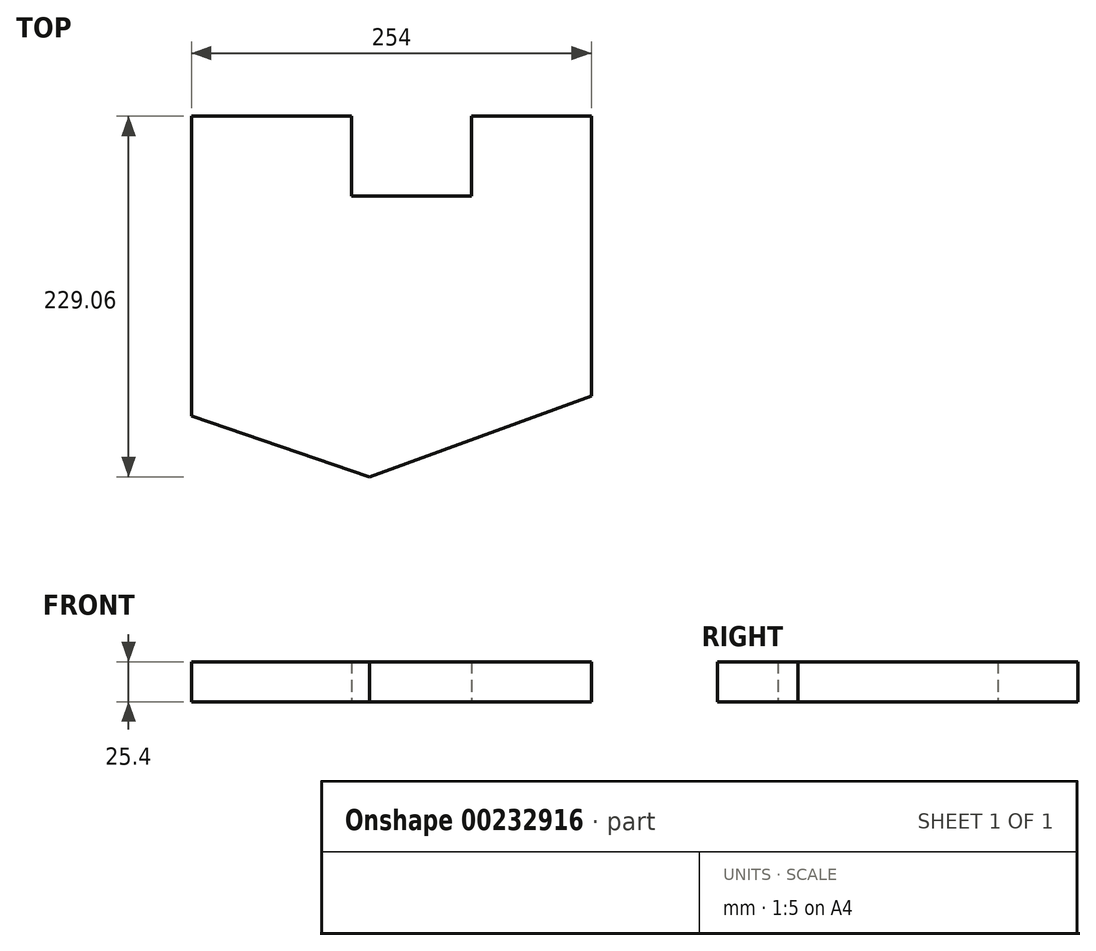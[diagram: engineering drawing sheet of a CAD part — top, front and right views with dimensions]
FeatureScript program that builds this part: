
annotation { "Feature Type Name" : "Feature", "Feature Type Description" : "" }
export const myFeature = defineFeature(function(context is Context, id is Id, definition is map)
    precondition{}
    {
        {
            var Q0;
            Q0=qCreatedBy(makeId("Top.planeOp"),FACE);
            var sketch = newSketch(context, id + "F0", { "sketchPlane" : qUnion([Q0])});
            skLineSegment(sketch, "E0", {"start": v(-68.2, 126.63) * mm, "end": v(-68.2, -63.87) * mm});
            skLineSegment(sketch, "E1", {"start": v(-68.2, 126.63) * mm, "end": v(33.4, 126.63) * mm});
            skLineSegment(sketch, "E2", {"start": v(33.4, 126.63) * mm, "end": v(33.4, 75.83) * mm});
            skLineSegment(sketch, "E3", {"start": v(33.4, 75.83) * mm, "end": v(109.6, 75.83) * mm});
            skLineSegment(sketch, "E4", {"start": v(109.6, 75.83) * mm, "end": v(109.6, 126.63) * mm});
            skLineSegment(sketch, "E5", {"start": v(109.6, 126.63) * mm, "end": v(185.8, 126.63) * mm});
            skLineSegment(sketch, "E6", {"start": v(185.8, 126.63) * mm, "end": v(185.8, -51.17) * mm});
            skLineSegment(sketch, "E7", {"start": v(185.8, -51.17) * mm, "end": v(19.14, -51.17) * mm});
            skLineSegment(sketch, "E8", {"start": v(185.8, -51.17) * mm, "end": v(44.98, -102.43) * mm});
            skLineSegment(sketch, "E9", {"start": v(-68.2, -63.87) * mm, "end": v(44.98, -102.43) * mm});
            skSolve(sketch);
        }
        {
            var Q0;
            Q0 = qSketchRegion(id + "F0", true);
            extrude(context, id + "F1", {"entities" : qUnion([Q0]), "depth" : 25.4 * mm});
        }
    });
